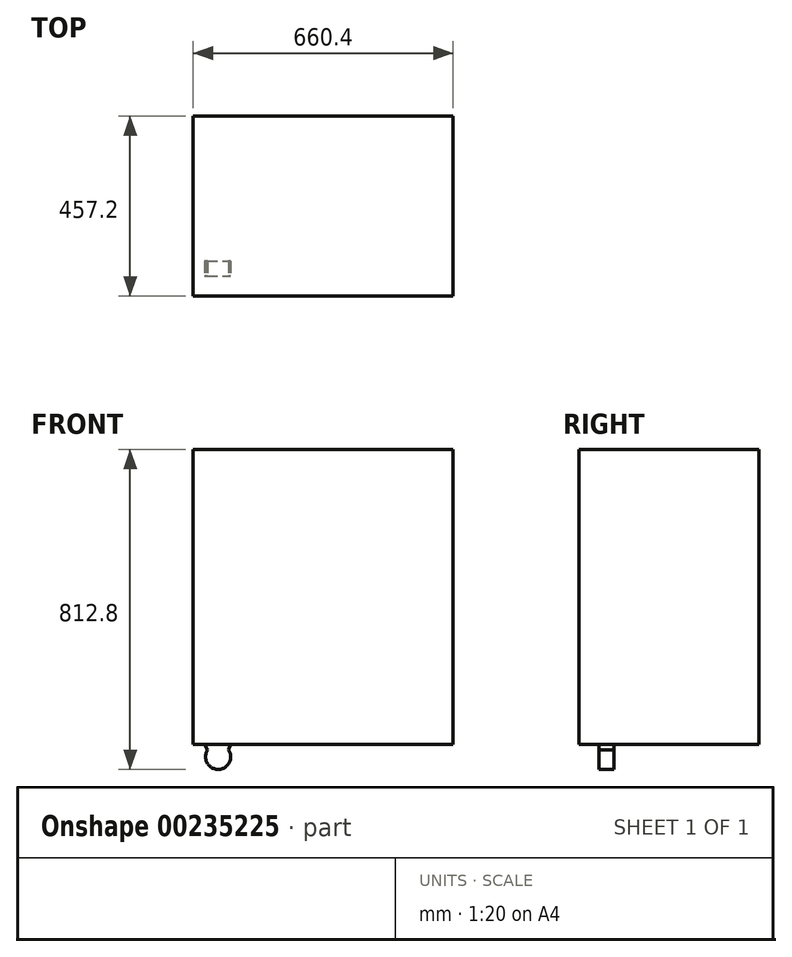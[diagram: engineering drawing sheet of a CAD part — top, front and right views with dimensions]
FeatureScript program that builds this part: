
annotation { "Feature Type Name" : "Feature", "Feature Type Description" : "" }
export const myFeature = defineFeature(function(context is Context, id is Id, definition is map)
    precondition{}
    {
        {
            var Q0;
            Q0=qCreatedBy(makeId("Front.planeOp"),FACE);
            var sketch = newSketch(context, id + "F0", { "sketchPlane" : qUnion([Q0])});
            skLineSegment(sketch, "E0.bottom", {"start": v(-330.2, 374.65) * mm, "end": v(330.2, 374.65) * mm});
            skLineSegment(sketch, "E0.top", {"start": v(-330.2, -374.65) * mm, "end": v(330.2, -374.65) * mm});
            skLineSegment(sketch, "E0.left", {"start": v(-330.2, 374.65) * mm, "end": v(-330.2, -374.65) * mm});
            skLineSegment(sketch, "E0.right", {"start": v(330.2, 374.65) * mm, "end": v(330.2, -374.65) * mm});
            skSolve(sketch);
        }
        {
            var Q0;
            Q0=makeQuery(id+"F0.imprint","IMPRINT",FACE,{"disambiguationData":[TD([[makeQuery(id+"F0.imprint","IMPRINT",EDGE,{"derivedFrom":sQuery(id+"F0.wireOp",EDGE,"E0.bottom")}),-1.0]])]});
            extrude(context, id + "F1", {"entities" : qUnion([Q0]), "depth" : 457.2 * mm});
        }
        {
            var Q0;
            Q0=makeQuery(id+"F1.opExtrude","CAP_FACE",FACE,{"disambiguationData":[OSD([sQuery(id+"F0.wireOp",EDGE,"E0.bottom"),sQuery(id+"F0.wireOp",EDGE,"E0.top"),sQuery(id+"F0.wireOp",EDGE,"E0.left"),sQuery(id+"F0.wireOp",EDGE,"E0.right")])],"isStart":false});
            cPlane(context, id + "F2", {"entities" : qUnion([Q0]), "cplaneType" : CPlaneType.OFFSET, "offset" : 50.8 * mm, "oppositeDirection" : true, "width" : 152.4 * mm, "height" : 152.4 * mm});
        }
        {
            var Q0;
            Q0=qCreatedBy(id+"F2.planeOp",FACE);
            var sketch = newSketch(context, id + "F3", { "sketchPlane" : qUnion([Q0])});
            skArc(sketch, "E1", {"start": v(-293.08, -388.73) * mm, "mid": v(-266.7, -438.15) * mm, "end": v(-240.32, -388.73) * mm});
            skLineSegment(sketch, "E2", {"start": v(-301.64, -374.65) * mm, "end": v(-235.1, -374.65) * mm});
            skLineSegment(sketch, "E3", {"start": v(-235.1, -374.65) * mm, "end": v(-240.32, -388.73) * mm});
            skLineSegment(sketch, "E4", {"start": v(-293.08, -388.73) * mm, "end": v(-301.64, -374.65) * mm});
            skSolve(sketch);
        }
        {
            var Q0;
            Q0 = qSketchRegion(id + "F3", true);
            extrude(context, id + "F4", {"entities" : qUnion([Q0]), "operationType" : NewBodyOperationType.ADD, "oppositeDirection" : true, "depth" : 38.1 * mm});
        }
    });
